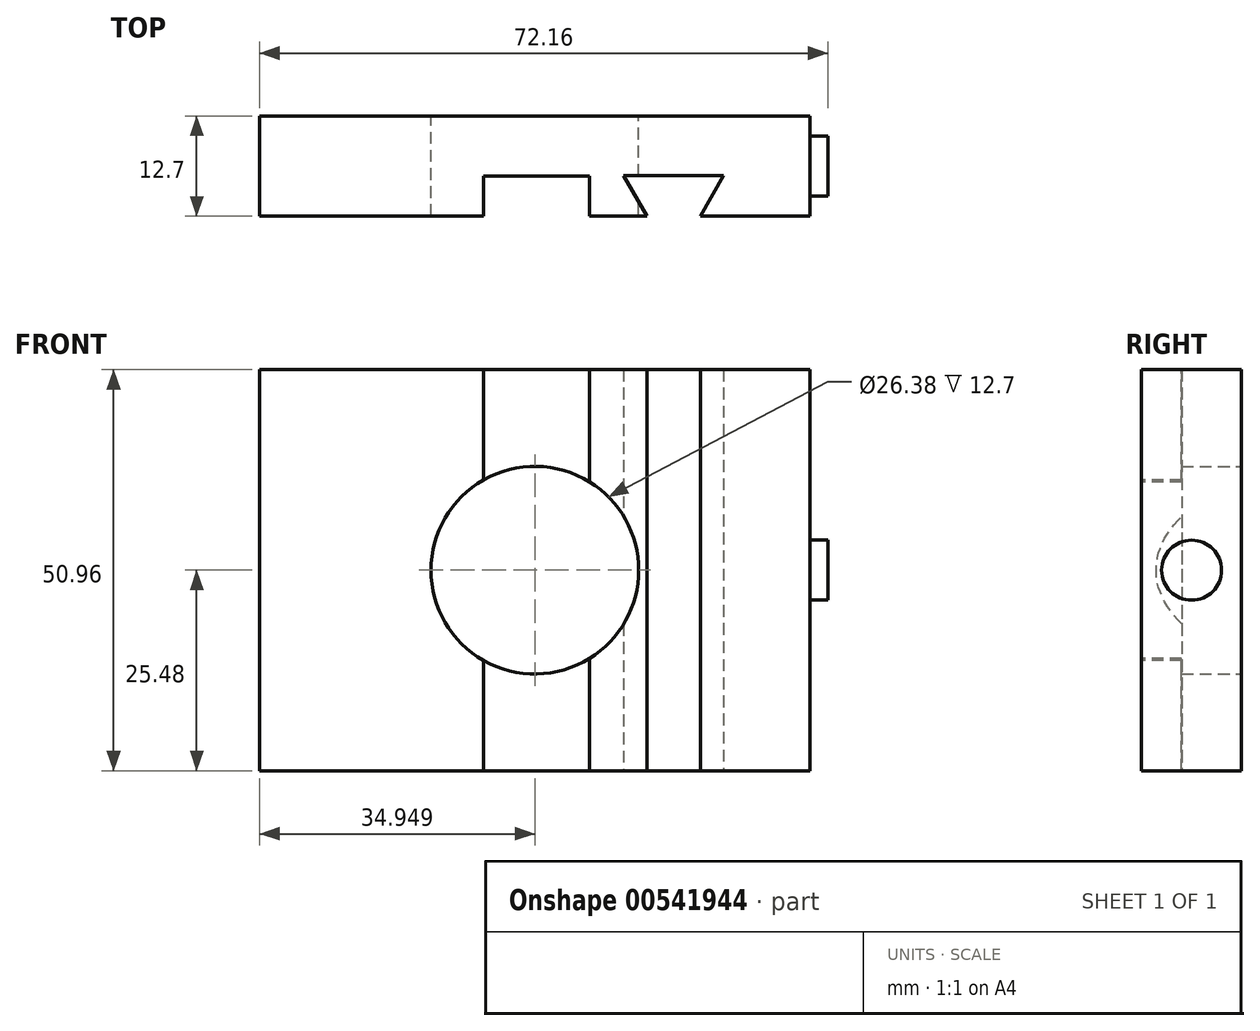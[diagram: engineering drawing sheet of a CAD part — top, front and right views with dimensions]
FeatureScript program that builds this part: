
annotation { "Feature Type Name" : "Feature", "Feature Type Description" : "" }
export const myFeature = defineFeature(function(context is Context, id is Id, definition is map)
    precondition{}
    {
        {
            var Q0;
            Q0=qCreatedBy(makeId("Front.planeOp"),FACE);
            var sketch = newSketch(context, id + "F0", { "sketchPlane" : qUnion([Q0])});
            skLineSegment(sketch, "E0.bottom", {"start": v(-35.16, 25.48) * mm, "end": v(34.74, 25.48) * mm});
            skLineSegment(sketch, "E0.top", {"start": v(-35.16, -25.48) * mm, "end": v(34.74, -25.48) * mm});
            skLineSegment(sketch, "E0.left", {"start": v(-35.16, 25.48) * mm, "end": v(-35.16, -25.48) * mm});
            skLineSegment(sketch, "E0.right", {"start": v(34.74, 25.48) * mm, "end": v(34.74, -25.48) * mm});
            skPoint(sketch, "E0.middle", {"position": v(-0.21, 0) * mm});
            skCircle(sketch, "E1", {"center": v(-0.21, 0) * mm, "radius": 13.2 * mm});
            skSolve(sketch);
        }
        {
            var Q0;
            Q0=makeQuery(id+"F0.imprint","IMPRINT",FACE,{"disambiguationData":[TD([[makeQuery(id+"F0.imprint","IMPRINT",EDGE,{"derivedFrom":sQuery(id+"F0.wireOp",EDGE,"E0.bottom")}),-1.0]])]});
            extrude(context, id + "F1", {"entities" : qUnion([Q0]), "depth" : 12.7 * mm, "offsetDistance" : 25.4 * mm});
        }
        {
            var Q0;
            Q0=makeQuery(id+"F1.opExtrude","CAP_FACE",FACE,{"disambiguationData":[OSD([sQuery(id+"F0.wireOp",EDGE,"E0.bottom"),sQuery(id+"F0.wireOp",EDGE,"E0.top"),sQuery(id+"F0.wireOp",EDGE,"E0.left"),sQuery(id+"F0.wireOp",EDGE,"E0.right"),sQuery(id+"F0.wireOp",EDGE,"E1")])],"isStart":false});
            var sketch = newSketch(context, id + "F2", { "sketchPlane" : qUnion([Q0])});
            skLineSegment(sketch, "E2", {"start": v(-6.74, 25.48) * mm, "end": v(-6.74, -25.48) * mm});
            skLineSegment(sketch, "E3", {"start": v(-6.74, -25.48) * mm, "end": v(6.74, -25.48) * mm});
            skLineSegment(sketch, "E4", {"start": v(6.74, -25.48) * mm, "end": v(6.74, 25.48) * mm});
            skLineSegment(sketch, "E5", {"start": v(6.74, 25.48) * mm, "end": v(-6.74, 25.48) * mm});
            skLineSegment(sketch, "E6", {"start": v(0, 23.58) * mm, "end": v(0, -25.48) * mm, "construction": true});
            skPoint(sketch, "E6.startSnap0", {"position": v(0, 25.48) * mm});
            skSolve(sketch);
        }
        {
            var Q0;
            {var subQ0=sQuery(id+"F2.wireOp",EDGE,"E5");Q0=makeQuery(id+"F2.imprint","IMPRINT",FACE,{"disambiguationData":[TD([[makeQuery(id+"F2.imprint","IMPRINT",EDGE,{"derivedFrom":subQ0}),-1.0]])]});}
            var Q1;
            {var subQ0=sQuery(id+"F2.wireOp",EDGE,"E3");Q1=makeQuery(id+"F2.imprint","IMPRINT",FACE,{"disambiguationData":[TD([[makeQuery(id+"F2.imprint","IMPRINT",EDGE,{"derivedFrom":subQ0}),1.0]])]});}
            extrude(context, id + "F3", {"entities" : qUnion([Q0, Q1]), "operationType" : NewBodyOperationType.REMOVE, "oppositeDirection" : true, "depth" : 5.08 * mm, "offsetDistance" : 25.4 * mm});
        }
        {
            var Q0;
            Q0=makeQuery(id+"F1.opExtrude","SWEPT_FACE",FACE,{"disambiguationData":[OSD([sQuery(id+"F0.wireOp",EDGE,"E0.top")])]});
            var sketch = newSketch(context, id + "F4", { "sketchPlane" : qUnion([Q0])});
            skLineSegment(sketch, "E7", {"start": v(14.04, 12.7) * mm, "end": v(11.07, 7.56) * mm});
            skLineSegment(sketch, "E8", {"start": v(11.07, 7.56) * mm, "end": v(23.77, 7.56) * mm});
            skLineSegment(sketch, "E9", {"start": v(23.77, 7.56) * mm, "end": v(20.8, 12.7) * mm});
            skLineSegment(sketch, "E10", {"start": v(20.8, 12.7) * mm, "end": v(14.04, 12.7) * mm});
            skSolve(sketch);
        }
        {
            var Q0;
            Q0=makeQuery(id+"F4.imprint","IMPRINT",FACE,{"disambiguationData":[TD([[makeQuery(id+"F4.imprint","IMPRINT",EDGE,{"derivedFrom":sQuery(id+"F4.wireOp",EDGE,"E7")}),1.0]])]});
            extrude(context, id + "F5", {"entities" : qUnion([Q0]), "operationType" : NewBodyOperationType.REMOVE, "endBound" : BoundingType.THROUGH_ALL, "oppositeDirection" : true, "depth" : 25.4 * mm, "offsetDistance" : 25.4 * mm});
        }
        {
            var Q0;
            Q0=makeQuery(id+"F1.opExtrude","SWEPT_FACE",FACE,{"disambiguationData":[OSD([sQuery(id+"F0.wireOp",EDGE,"E0.right")])]});
            var sketch = newSketch(context, id + "F6", { "sketchPlane" : qUnion([Q0])});
            skCircle(sketch, "E11", {"center": v(-6.35, 0) * mm, "radius": 3.81 * mm});
            skPoint(sketch, "E11.centerSnap0", {"position": v(-6.35, 25.48) * mm});
            skPoint(sketch, "E11.centerSnap1", {"position": v(0, 0) * mm});
            skSolve(sketch);
        }
        {
            var Q0;
            Q0=makeQuery(id+"F6.imprint","IMPRINT",FACE,{"disambiguationData":[TD([[makeQuery(id+"F6.imprint","IMPRINT",EDGE,{"derivedFrom":sQuery(id+"F6.wireOp",EDGE,"E11")}),1.0]])]});
            extrude(context, id + "F7", {"entities" : qUnion([Q0]), "operationType" : NewBodyOperationType.ADD, "depth" : 2.26 * mm, "offsetDistance" : 25.4 * mm});
        }
    });
